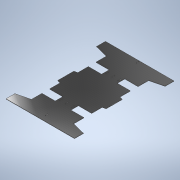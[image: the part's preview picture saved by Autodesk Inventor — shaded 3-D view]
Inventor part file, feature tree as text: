
AUTODESK INVENTOR PART (.ipt)
format: ipt  version: 2021 (Build 250183000, 183)  size: 317,440 bytes
history: native  units: mm
features: other x13, reference x11, sketch x6, extrude x4
ambient origin geometry x8: Origin, YZ Plane, XZ Plane, XY Plane, X Axis, Y Axis, Z Axis, Center Point
bodies: Solid1 (feature_tree)
feature tree (34):
  extrude  "Extrusion1"  Depth=3.0mm
  extrude  "Extrusion2"  Depth=35.0mm
  sketch  "Sketch3"  dims[d27=35.0mm d28=35.0mm]
  sketch  "Sketch4"  dims[d29=35.0mm d30=35.0mm]
  extrude  "Extrusion7"  Depth=35.0mm
  extrude  "Extrusion8"  Depth=35.0mm
  sketch  "Sketch1"  dims[d12=3.0mm d13=0.0mm d16=80.0mm]
  sketch  "Sketch2"  dims[d23=65.0mm d26=35.0mm]
  sketch  "Sketch7"  dims[d31=35.0mm]
  reference  "Reference4"
  reference  "Reference5"
  reference  "Reference6"
  reference  "Reference7"
  reference  "Reference8"
  reference  "Reference11"
  reference  "Reference12"
  reference  "Reference13"
  reference  "Reference14"
  reference  "Reference15"
  reference  "Reference16"
  sketch  "Sketch8"  dims[d32=10.0mm d33=0.0mm d34=20.0mm d35=40.0mm d36=20.0mm d37=20.0mm d38=20.0mm d44=0.45mm d53=6.0mm d54=6.0mm d55=6.0mm d56=6.0mm d57=6.0mm d58=6.0mm d59=6.0mm d60=6.0mm d61=6.0mm d62=6.0mm d63=6.0mm d64=6.0mm d65=6.0mm d66=6.0mm d67=6.0mm d68=6.0mm d69=10.0mm d70=0.0mm d73=0.0mm d74=0.0mm]
  parser-record x1  (decoder bookkeeping rows leaked as tree rows — omitted from the tree; the rows remain in map.json)
  other  "assembly.iam"
  other  "hexagonal_nut_autolock_M6:15"
  other  "hexagonal_nut_autolock_M6:16"
  other  "hexagonal_nut_autolock_M6:9"
  other  "hexagonal_nut_autolock_M6:14"
  other  "hexagonal_nut_autolock_M6:11"
  other  "hexagonal_nut_autolock_M6:2"
  other  "hexagonal_nut_autolock_M6:8"
  other  "hexagonal_nut_autolock_M6:1"
  other  "hexagonal_nut_autolock_M6:7"
  other  "hexagonal_nut_autolock_M6:5"
  other  "hexagonal_nut_autolock_M6:4"
note: 1 file-system path scrubbed to <path> (originals preserved in map.json)
